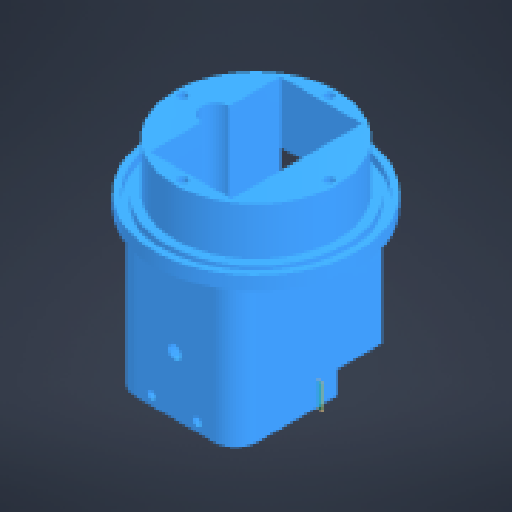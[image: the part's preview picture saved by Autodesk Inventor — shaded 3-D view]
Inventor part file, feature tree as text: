
AUTODESK INVENTOR PART (.ipt)
format: ipt  version: 2024 (Build 280153000, 153)  size: 291,328 bytes
history: native  units: mm
features: reference x15, other x9, extrude x6, sketch x6, fillet x1, projected_geometry x1, imported_body x1
ambient origin geometry x8: Origin, YZ Plane, XZ Plane, XY Plane, X Axis, Y Axis, Z Axis, Center Point
bodies: Body1 (feature_tree)
feature tree (39):
  other  "Твердое тело1"
  extrude  "Выдавливание1"  Depth=3.0mm TaperAngle=0.0deg
  extrude  "Выдавливание2"  Depth=6.25mm TaperAngle=0.0deg
  extrude  "Выдавливание3"  Depth=18.25mm TaperAngle=0.0deg
  other  "РабПлоскость1"
  extrude  "Выдавливание4"  Depth=1.5mm
  fillet  "Сопряжение1"  Radius=37.5mm
  extrude  "Выдавливание5"  Depth=8.0mm
  other  "РабПлоскость2"
  extrude  "Выдавливание6"  Depth=4.0mm
  sketch  "Эскиз1"
  reference  "Ссылка1"
  reference  "Ссылка2"
  reference  "Ссылка3"
  sketch  "Эскиз3"
  sketch  "Эскиз4"
  sketch  "Эскиз5"
  reference  "Ссылка4"
  reference  "Ссылка5"
  reference  "Ссылка6"
  reference  "Ссылка7"
  reference  "Ссылка8"
  reference  "Ссылка9"
  reference  "Ссылка10"
  sketch  "Эскиз6"
  projected_geometry  "Спроецированная петля1"
  reference  "Ссылка11"
  reference  "Ссылка12"
  reference  "Ссылка13"
  sketch  "Эскиз7"
  reference  "Ссылка14"
  reference  "Ссылка15"
  imported_body  "БазТело1"
  parser-record x2  (decoder bookkeeping rows leaked as tree rows — omitted from the tree; the rows remain in map.json)
  other  "bushing_asm.iam"
  other  "ring:1"
  other  "manipulator.iam"
  other  "servo_80kg_base:1"
note: 2 file-system paths scrubbed to <path> (originals preserved in map.json)
